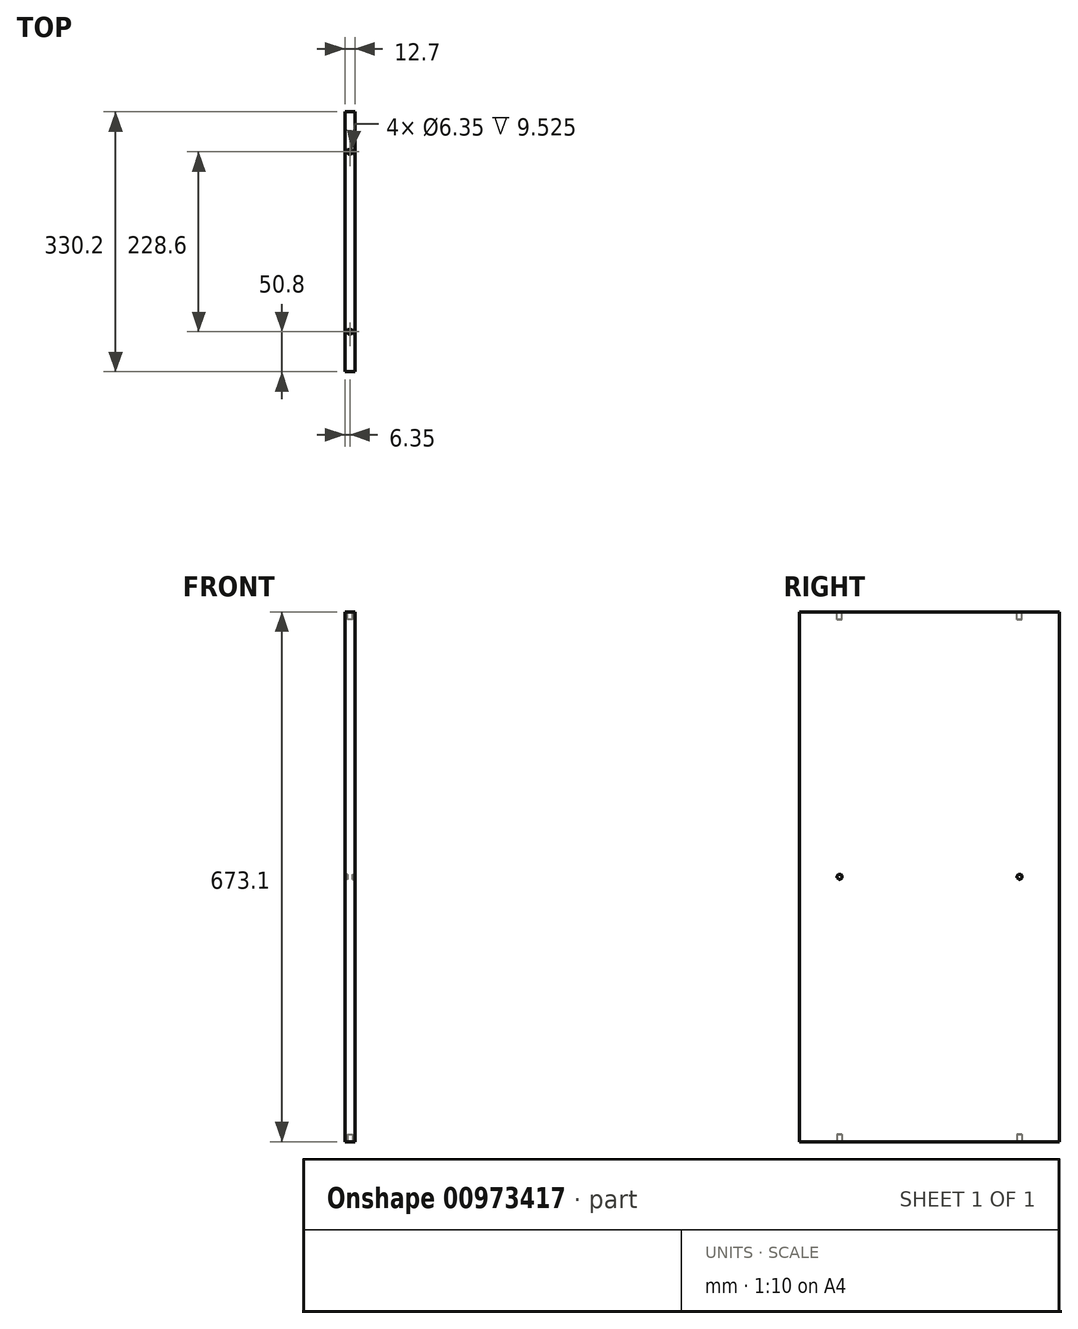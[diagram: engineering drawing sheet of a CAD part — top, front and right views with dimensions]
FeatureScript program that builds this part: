
annotation { "Feature Type Name" : "Feature", "Feature Type Description" : "" }
export const myFeature = defineFeature(function(context is Context, id is Id, definition is map)
    precondition{}
    {
        {
            var Q0;
            Q0=qCreatedBy(makeId("Top.planeOp"),FACE);
            var sketch = newSketch(context, id + "F0", { "sketchPlane" : qUnion([Q0])});
            skLineSegment(sketch, "E0.bottom", {"start": v(0, 0) * mm, "end": v(12.7, 0) * mm});
            skLineSegment(sketch, "E0.top", {"start": v(0, 330.2) * mm, "end": v(12.7, 330.2) * mm});
            skLineSegment(sketch, "E0.left", {"start": v(0, 0) * mm, "end": v(0, 330.2) * mm});
            skLineSegment(sketch, "E0.right", {"start": v(12.7, 0) * mm, "end": v(12.7, 330.2) * mm});
            skSolve(sketch);
        }
        {
            var Q0;
            Q0=makeQuery(id+"F0.imprint","IMPRINT",FACE,{"disambiguationData":[TD([[makeQuery(id+"F0.imprint","IMPRINT",EDGE,{"derivedFrom":sQuery(id+"F0.wireOp",EDGE,"E0.bottom")}),1.0]])]});
            extrude(context, id + "F1", {"entities" : qUnion([Q0]), "depth" : 673.1 * mm, "offsetDistance" : 25.4 * mm});
        }
        {
            var Q0;
            Q0=makeQuery(id+"F1.opExtrude","CAP_FACE",FACE,{"disambiguationData":[OSD([sQuery(id+"F0.wireOp",EDGE,"E0.bottom"),sQuery(id+"F0.wireOp",EDGE,"E0.top"),sQuery(id+"F0.wireOp",EDGE,"E0.left"),sQuery(id+"F0.wireOp",EDGE,"E0.right")])],"isStart":true});
            var sketch = newSketch(context, id + "F2", { "sketchPlane" : qUnion([Q0])});
            skCircle(sketch, "E1", {"center": v(6.35, -50.8) * mm, "radius": 3.18 * mm});
            skCircle(sketch, "E2", {"center": v(6.35, -279.4) * mm, "radius": 3.18 * mm});
            skSolve(sketch);
        }
        {
            var Q0;
            Q0=qSketchRegion(id+"F2",true);
            extrude(context, id + "F3", {"entities" : qUnion([Q0]), "operationType" : NewBodyOperationType.REMOVE, "oppositeDirection" : true, "depth" : 9.52 * mm, "offsetDistance" : 25.4 * mm});
        }
        {
            var Q0;
            Q0=makeQuery(id+"F1.opExtrude","CAP_FACE",FACE,{"disambiguationData":[OSD([sQuery(id+"F0.wireOp",EDGE,"E0.bottom"),sQuery(id+"F0.wireOp",EDGE,"E0.top"),sQuery(id+"F0.wireOp",EDGE,"E0.left"),sQuery(id+"F0.wireOp",EDGE,"E0.right")])],"isStart":false});
            var sketch = newSketch(context, id + "F4", { "sketchPlane" : qUnion([Q0])});
            skCircle(sketch, "E3", {"center": v(6.35, 279.4) * mm, "radius": 3.18 * mm});
            skCircle(sketch, "E4", {"center": v(6.35, 50.8) * mm, "radius": 3.18 * mm});
            skSolve(sketch);
        }
        {
            var Q0;
            Q0=qSketchRegion(id+"F4",true);
            extrude(context, id + "F5", {"entities" : qUnion([Q0]), "operationType" : NewBodyOperationType.REMOVE, "oppositeDirection" : true, "depth" : 9.52 * mm, "offsetDistance" : 25.4 * mm});
        }
        {
            var Q0;
            Q0=makeQuery(id+"F1.opExtrude","SWEPT_FACE",FACE,{"disambiguationData":[OSD([sQuery(id+"F0.wireOp",EDGE,"E0.left")])]});
            var sketch = newSketch(context, id + "F6", { "sketchPlane" : qUnion([Q0])});
            skCircle(sketch, "E5", {"center": v(-279.4, 336.55) * mm, "radius": 3.18 * mm});
            skCircle(sketch, "E6", {"center": v(-50.8, 336.55) * mm, "radius": 3.18 * mm});
            skSolve(sketch);
        }
        {
            var Q0;
            Q0=makeQuery(id+"F1.opExtrude","SWEPT_FACE",FACE,{"disambiguationData":[OSD([sQuery(id+"F0.wireOp",EDGE,"E0.right")])]});
            var sketch = newSketch(context, id + "F7", { "sketchPlane" : qUnion([Q0])});
            skCircle(sketch, "E7", {"center": v(50.8, 336.55) * mm, "radius": 3.18 * mm});
            skCircle(sketch, "E8", {"center": v(279.4, 336.55) * mm, "radius": 3.18 * mm});
            skSolve(sketch);
        }
        {
            var Q0;
            Q0 = qSketchRegion(id + "F6", true);
            extrude(context, id + "F8", {"entities" : qUnion([Q0]), "operationType" : NewBodyOperationType.REMOVE, "oppositeDirection" : true, "depth" : 3.17 * mm, "offsetDistance" : 25.4 * mm});
        }
        {
            var Q0;
            Q0 = qSketchRegion(id + "F7", true);
            extrude(context, id + "F9", {"entities" : qUnion([Q0]), "operationType" : NewBodyOperationType.REMOVE, "oppositeDirection" : true, "depth" : 3.17 * mm, "offsetDistance" : 25.4 * mm});
        }
    });
